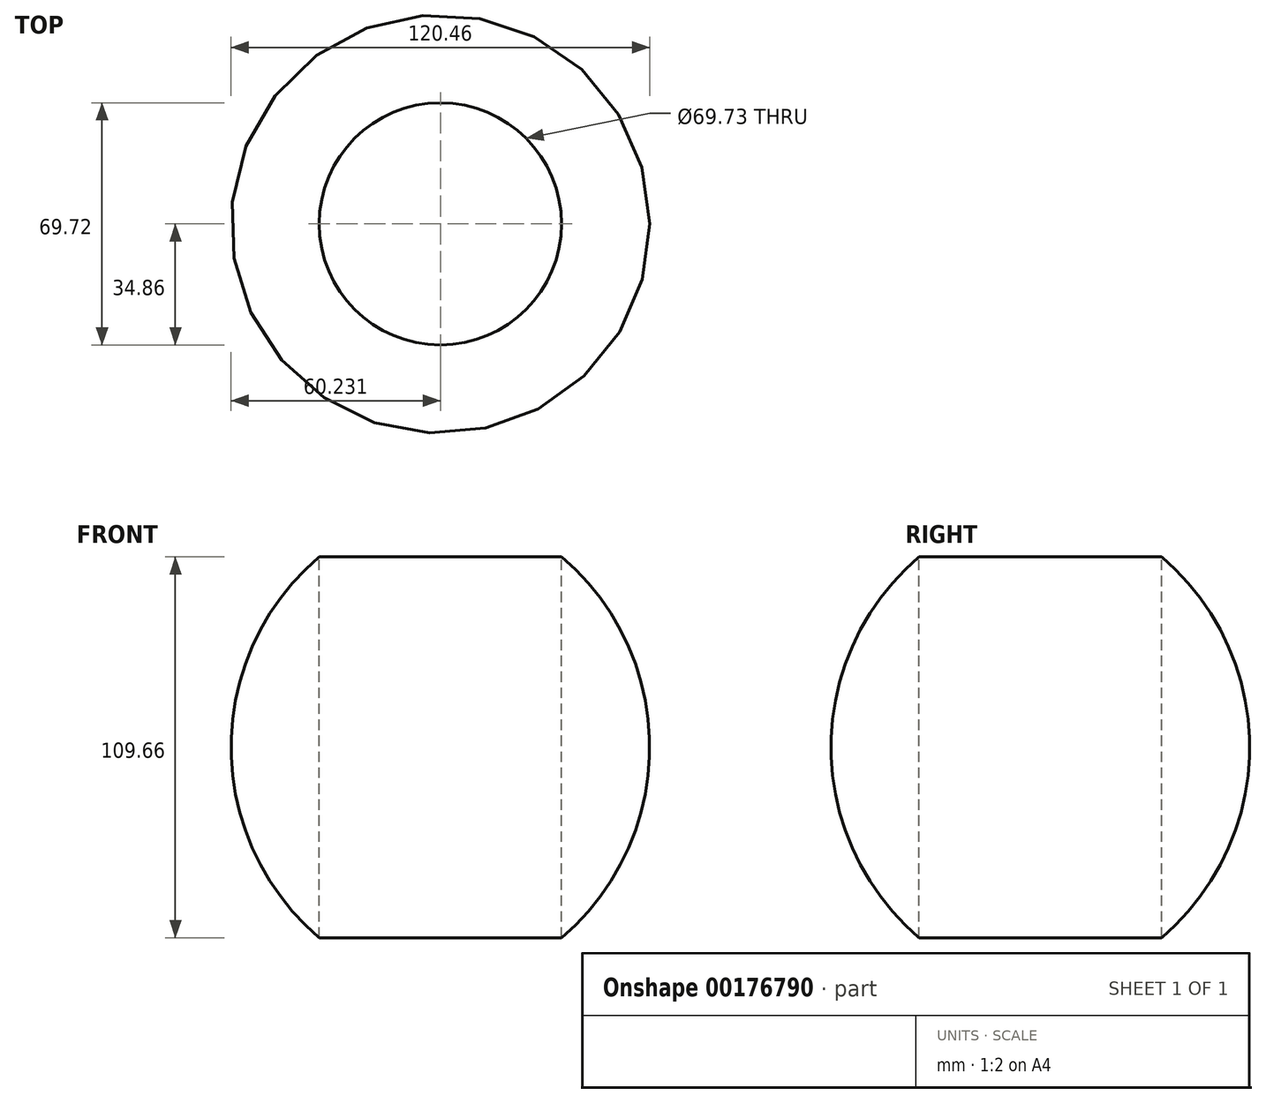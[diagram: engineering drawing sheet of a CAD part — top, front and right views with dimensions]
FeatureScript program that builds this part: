
annotation { "Feature Type Name" : "Feature", "Feature Type Description" : "" }
export const myFeature = defineFeature(function(context is Context, id is Id, definition is map)
    precondition{}
    {
        {
            var Q0;
            Q0=qCreatedBy(makeId("Front.planeOp"),FACE);
            var sketch = newSketch(context, id + "F0", { "sketchPlane" : qUnion([Q0])});
            skLineSegment(sketch, "E0", {"start": v(-50.5, 56.47) * mm, "end": v(-50.5, -51.1) * mm});
            skLineSegment(sketch, "E1", {"start": v(-15.64, 56.17) * mm, "end": v(-15.64, -53.49) * mm});
            skArc(sketch, "E2", {"start": v(-15.64, -53.49) * mm, "mid": v(9.72, 1.34) * mm, "end": v(-15.64, 56.17) * mm});
            skSolve(sketch);
        }
        {
            var Q0;
            Q0=makeQuery(id+"F0.imprint","IMPRINT",FACE,{"disambiguationData":[TD([[makeQuery(id+"F0.imprint","IMPRINT",EDGE,{"derivedFrom":sQuery(id+"F0.wireOp",EDGE,"E1")}),1.0]])]});
            var Q1;
            Q1=sQuery(id+"F0.wireOp",EDGE,"E0");
            revolve(context, id + "F1", {"entities" : qUnion([Q0]), "axis" : qUnion([Q1]), "revolveType" : RevolveType.FULL});
        }
    });
